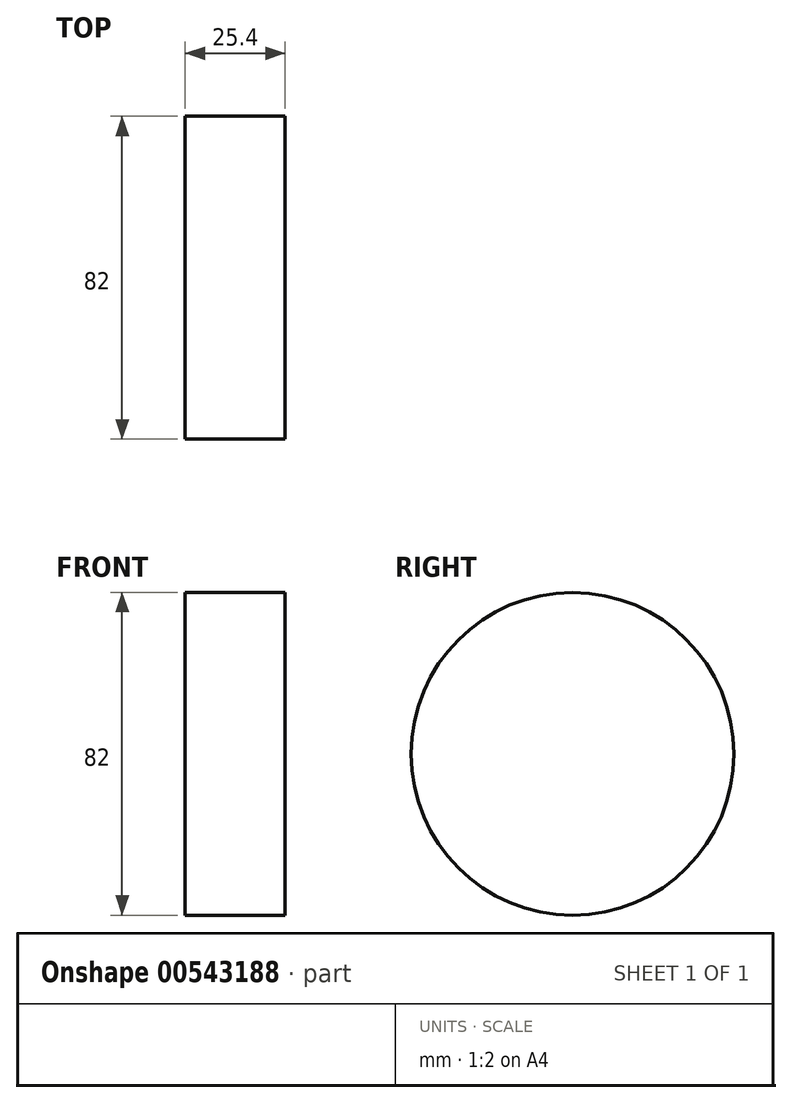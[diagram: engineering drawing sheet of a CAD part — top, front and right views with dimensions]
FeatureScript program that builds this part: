
annotation { "Feature Type Name" : "Feature", "Feature Type Description" : "" }
export const myFeature = defineFeature(function(context is Context, id is Id, definition is map)
    precondition{}
    {
        {
            var Q0;
            Q0=qCreatedBy(makeId("Right.planeOp"),FACE);
            var sketch = newSketch(context, id + "F0", { "sketchPlane" : qUnion([Q0])});
            skCircle(sketch, "E0", {"center": v(0, 0) * mm, "radius": 41 * mm});
            skSolve(sketch);
        }
        {
            var Q0;
            Q0=makeQuery(id+"F0.imprint","IMPRINT",FACE,{"disambiguationData":[TD([[makeQuery(id+"F0.imprint","IMPRINT",EDGE,{"derivedFrom":sQuery(id+"F0.wireOp",EDGE,"E0")}),1.0]])]});
            extrude(context, id + "F1", {"entities" : qUnion([Q0]), "depth" : 25.4 * mm, "offsetDistance" : 25.4 * mm});
        }
    });
